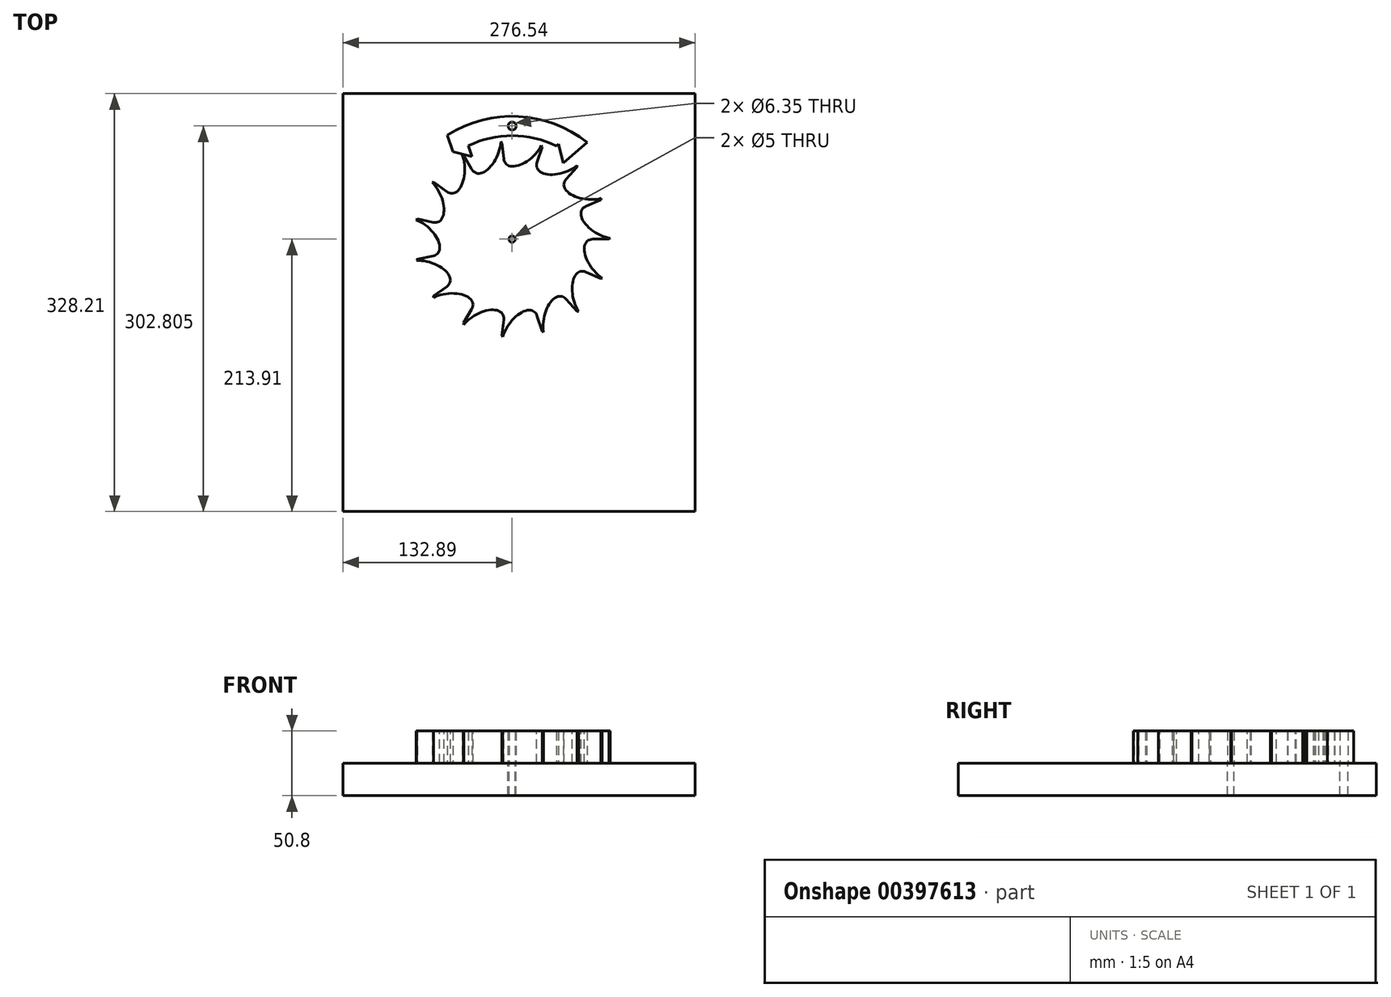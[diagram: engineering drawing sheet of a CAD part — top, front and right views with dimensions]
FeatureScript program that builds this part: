
annotation { "Feature Type Name" : "Feature", "Feature Type Description" : "" }
export const myFeature = defineFeature(function(context is Context, id is Id, definition is map)
    precondition{}
    {
        {
            var Q0;
            Q0=qCreatedBy(makeId("Top.planeOp"),FACE);
            var sketch = newSketch(context, id + "F0", { "sketchPlane" : qUnion([Q0])});
            skCircle(sketch, "E0", {"center": v(0, 0) * mm, "radius": 76.2 * mm, "construction": true});
            skCircle(sketch, "E1", {"center": v(0, 0) * mm, "radius": 95.25 * mm, "construction": true});
            skCircle(sketch, "E2", {"center": v(0, 0) * mm, "radius": 57.15 * mm, "construction": true});
            skLineSegment(sketch, "E3", {"start": v(0, 0) * mm, "end": v(-38.48, 66.66) * mm, "construction": true});
            skLineSegment(sketch, "E4", {"start": v(-104.67, 27.56) * mm, "end": v(65.84, 126) * mm, "construction": true});
            skLineSegment(sketch, "E5", {"start": v(0, 0) * mm, "end": v(-46.24, 33.6) * mm, "construction": true});
            skLineSegment(sketch, "E6", {"start": v(-96.61, 34.43) * mm, "end": v(96.61, 141.54) * mm, "construction": true});
            skPoint(sketch, "E7", {"position": v(0, 87.99) * mm});
            skPoint(sketch, "E7.positionSnap0", {"position": v(0, 87.99) * mm});
            skLineSegment(sketch, "E8", {"start": v(-38.1, 66) * mm, "end": v(-39.17, 66.28) * mm});
            skPoint(sketch, "E9", {"position": v(-51.37, 37.32) * mm});
            skPoint(sketch, "E10", {"position": v(-37.64, 60.11) * mm});
            skLineSegment(sketch, "E11.trimOffspring", {"start": v(-40.07, 69.4) * mm, "end": v(-47.63, 82.49) * mm});
            skEllipticalArc(sketch, "E12.trimOffspring", {});
            skLineSegment(sketch, "E13.trimOffspring", {"start": v(-51.37, 37.32) * mm, "end": v(-61.65, 44.79) * mm});
            skCircle(sketch, "E14", {"center": v(0, 0) * mm, "radius": 2.5 * mm});
            skLineSegment(sketch, "E15", {"start": v(0, 0) * mm, "end": v(61, 105.66) * mm, "construction": true});
            skLineSegment(sketch, "E16.1.0", {"start": v(-61.65, 44.79) * mm, "end": v(-62.74, 44.62) * mm});
            skEllipticalArc(sketch, "E16.1.1", {});
            skLineSegment(sketch, "E16.1.2", {"start": v(-62.11, 13.2) * mm, "end": v(-74.53, 15.84) * mm});
            skLineSegment(sketch, "E16.2.0", {"start": v(-74.53, 15.84) * mm, "end": v(-75.46, 15.24) * mm});
            skEllipticalArc(sketch, "E16.2.1", {});
            skLineSegment(sketch, "E16.2.2", {"start": v(-62.11, -13.2) * mm, "end": v(-74.53, -15.84) * mm});
            skEllipticalArc(sketch, "E17.3.3.0", {});
            skLineSegment(sketch, "E17.7.3.0", {"start": v(-51.37, -37.32) * mm, "end": v(-61.65, -44.79) * mm});
            skLineSegment(sketch, "E17.9.3.0", {"start": v(-74.53, -15.84) * mm, "end": v(-75.14, -16.77) * mm});
            skEllipticalArc(sketch, "E17.3.4.0", {});
            skLineSegment(sketch, "E17.7.4.0", {"start": v(-31.75, -55) * mm, "end": v(-38.1, -66) * mm});
            skLineSegment(sketch, "E17.9.4.0", {"start": v(-61.65, -44.79) * mm, "end": v(-61.82, -45.88) * mm});
            skEllipticalArc(sketch, "E17.3.5.0", {});
            skLineSegment(sketch, "E17.7.5.0", {"start": v(-6.64, -63.15) * mm, "end": v(-7.97, -75.78) * mm});
            skLineSegment(sketch, "E17.9.5.0", {"start": v(-38.1, -66) * mm, "end": v(-37.81, -67.06) * mm});
            skEllipticalArc(sketch, "E17.3.6.0", {});
            skLineSegment(sketch, "E17.7.6.0", {"start": v(19.62, -60.4) * mm, "end": v(23.55, -72.47) * mm});
            skLineSegment(sketch, "E17.9.6.0", {"start": v(-7.97, -75.78) * mm, "end": v(-7.27, -76.64) * mm});
            skEllipticalArc(sketch, "E17.3.7.0", {});
            skLineSegment(sketch, "E17.7.7.0", {"start": v(42.49, -47.19) * mm, "end": v(50.99, -56.63) * mm});
            skLineSegment(sketch, "E17.9.7.0", {"start": v(23.55, -72.47) * mm, "end": v(24.53, -72.97) * mm});
            skEllipticalArc(sketch, "E17.3.8.0", {});
            skLineSegment(sketch, "E17.7.8.0", {"start": v(58.01, -25.83) * mm, "end": v(69.61, -31) * mm});
            skLineSegment(sketch, "E17.9.8.0", {"start": v(50.99, -56.63) * mm, "end": v(52.1, -56.69) * mm});
            skEllipticalArc(sketch, "E17.3.9.0", {});
            skLineSegment(sketch, "E17.7.9.0", {"start": v(63.5, 0) * mm, "end": v(76.2, 0) * mm});
            skLineSegment(sketch, "E17.9.9.0", {"start": v(69.61, -31) * mm, "end": v(70.64, -30.6) * mm});
            skEllipticalArc(sketch, "E17.3.10.0", {});
            skLineSegment(sketch, "E17.7.10.0", {"start": v(58.01, 25.83) * mm, "end": v(69.61, 31) * mm});
            skLineSegment(sketch, "E17.9.10.0", {"start": v(76.2, 0) * mm, "end": v(76.98, 0.78) * mm});
            skEllipticalArc(sketch, "E17.3.11.0", {});
            skLineSegment(sketch, "E17.7.11.0", {"start": v(42.49, 47.19) * mm, "end": v(50.99, 56.63) * mm});
            skLineSegment(sketch, "E17.9.11.0", {"start": v(69.61, 31) * mm, "end": v(70, 32.03) * mm});
            skEllipticalArc(sketch, "E17.3.12.0", {});
            skLineSegment(sketch, "E17.7.12.0", {"start": v(19.62, 60.4) * mm, "end": v(23.55, 72.47) * mm});
            skLineSegment(sketch, "E17.9.12.0", {"start": v(50.99, 56.63) * mm, "end": v(50.93, 57.73) * mm});
            skEllipticalArc(sketch, "E17.3.13.0", {});
            skLineSegment(sketch, "E17.7.13.0", {"start": v(-6.64, 63.15) * mm, "end": v(-7.97, 75.78) * mm});
            skLineSegment(sketch, "E17.9.13.0", {"start": v(23.55, 72.47) * mm, "end": v(23.05, 73.46) * mm});
            skEllipticalArc(sketch, "E17.3.14.0", {});
            skLineSegment(sketch, "E17.7.14.0", {"start": v(-31.75, 55) * mm, "end": v(-38.1, 66) * mm});
            skLineSegment(sketch, "E17.9.14.0", {"start": v(-7.97, 75.78) * mm, "end": v(-8.82, 76.48) * mm});
            const initialGuessF0  = {"E12.trimOffspring": [-0.04789060166335672, 0.05569995491011367, 0.03374826068931686, -0.999430365208325, 0.019781070479592194, 0.010620790046448907, 5.88684132578572, 2.1170960990921337], "E16.1.1": [-0.06640545429294378, 0.03140557824359797, 0.43733552198891873, -0.8992984161037314, 0.01978107047959219, 0.010620790046448905, 5.88684132578572, 2.117096099092134], "E16.2.1": [-0.07343820060066757, 0.001680891788042732, 0.7653034984681489, -0.6436696009851731, 0.019781070479592194, 0.010620790046448907, 5.886841325785718, 2.1170960990921346], "E17.3.3.0": [-0.0677728148594282, -0.028334436128087503, 0.9609435474982175, -0.27674446430153027, 0.019781070479592194, 0.010620790046448907, 5.88684132578572, 2.117096099092134], "E17.3.4.0": [-0.05038889373229961, -0.05345048262740028, 0.9904277272677787, 0.13803230440437778, 0.019781070479592194, 0.010620790046448907, 5.88684132578572, 2.1170960990921346], "E17.3.5.0": [-0.02429227511012787, -0.06932445509804504, 0.8486579552393103, 0.5289420336946504, 0.019781070479592194, 0.010620790046448907, 5.88684132578572, 2.117096099092134], "E17.3.6.0": [0.006004698566976163, -0.07321159948933473, 0.5601475129344807, 0.8283928800715973, 0.019781070479592194, 0.010620790046448907, 5.886841325785721, 2.1170960990921337], "E17.3.7.0": [0.03526340531087609, -0.06443979322241714, 0.17478247686287926, 0.9846070717711087, 0.019781070479592194, 0.010620790046448907, 5.88684132578572, 2.117096099092134], "E17.3.8.0": [0.058424748918545454, -0.04452576129020056, -0.24080403730726763, 0.9705737558869599, 0.019781070479592194, 0.010620790046448907, 5.88684132578572, 2.117096099092134], "E17.3.9.0": [0.07148392266601725, -0.016912820727065802, -0.6147533457909872, 0.7887194202241931, 0.019781070479592194, 0.010620790046448907, 5.88684132578572, 2.1170960990921346], "E17.3.10.0": [0.07218287677348459, 0.013624500187931342, -0.8824062159286269, 0.47048833151367486, 0.019781070479592194, 0.010620790046448907, 5.88684132578572, 2.1170960990921337], "E17.3.11.0": [0.06040075572596765, 0.041806021245736694, -0.9974830349233995, 0.07090553603213468, 0.019781070479592194, 0.010620790046448907, 5.88684132578572, 2.117096099092134], "E17.3.12.0": [0.0381747952897915, 0.06275890143437435, -0.9400859753310279, -0.34093747078593484, 0.019781070479592194, 0.010620790046448907, 5.88684132578572, 2.1170960990921337], "E17.3.13.0": [0.0093480659408827, 0.07286019741828806, -0.7201395101909495, -0.6938292915854298, 0.019781070479592194, 0.010620790046448907, 5.88684132578572, 2.117096099092134], "E17.3.14.0": [-0.021095028933717657, 0.07036330335446608, -0.37567438147679133, -0.9267517246285708, 0.019781070479592194, 0.010620790046448907, 5.886841325785721, 2.1170960990921337]};
            skSetInitialGuess(sketch, initialGuessF0);
            skSolve(sketch);
        }
        {
            var Q0;
            Q0=qSketchRegion(id+"F0",true);
            extrude(context, id + "F1", {"entities" : qUnion([Q0]), "depth" : 25.4 * mm});
        }
        {
            var Q0;
            Q0=qCreatedBy(makeId("Top.planeOp"),FACE);
            var sketch = newSketch(context, id + "F2", { "sketchPlane" : qUnion([Q0])});
            skLineSegment(sketch, "E18", {"start": v(-41.75, 72.3) * mm, "end": v(0, 0) * mm, "construction": true});
            skLineSegment(sketch, "E19", {"start": v(0, 0) * mm, "end": v(41.8, 72.41) * mm, "construction": true});
            skCircle(sketch, "E20", {"center": v(0, 0) * mm, "radius": 76.99 * mm, "construction": true});
            skLineSegment(sketch, "E21", {"start": v(-38.5, 66.67) * mm, "end": v(0, 88.9) * mm, "construction": true});
            skLineSegment(sketch, "E22", {"start": v(0, 88.9) * mm, "end": v(38.5, 66.67) * mm, "construction": true});
            skLineSegment(sketch, "E23", {"start": v(0, 0) * mm, "end": v(-44.19, 90.6) * mm, "construction": true});
            skLineSegment(sketch, "E24", {"start": v(0, 0) * mm, "end": v(-56.37, 83.56) * mm, "construction": true});
            skLineSegment(sketch, "E25", {"start": v(0, 88.9) * mm, "end": v(-127.8, 129.79) * mm, "construction": true});
            skLineSegment(sketch, "E26", {"start": v(0, 88.9) * mm, "end": v(-28.48, -42.22) * mm, "construction": true});
            skLineSegment(sketch, "E27", {"start": v(0, 88.9) * mm, "end": v(130.35, 25.32) * mm, "construction": true});
            skLineSegment(sketch, "E28", {"start": v(0, 88.9) * mm, "end": v(120.23, 7.8) * mm, "construction": true});
            skLineSegment(sketch, "E29", {"start": v(0, 0) * mm, "end": v(48.31, 99.05) * mm, "construction": true});
            skLineSegment(sketch, "E30", {"start": v(0, 0) * mm, "end": v(61.63, 91.36) * mm, "construction": true});
            skLineSegment(sketch, "E31", {"start": v(-46.4, 68.8) * mm, "end": v(-31.62, 64.83) * mm});
            skPoint(sketch, "E32", {"position": v(-38.5, 66.67) * mm});
            skLineSegment(sketch, "E33", {"start": v(-46.4, 68.8) * mm, "end": v(-50.8, 81.6) * mm});
            skLineSegment(sketch, "E34", {"start": v(-31.62, 64.83) * mm, "end": v(-34.54, 73.3) * mm});
            skLineSegment(sketch, "E35", {"start": v(36.37, 74.58) * mm, "end": v(40.33, 59.8) * mm});
            skPoint(sketch, "E36", {"position": v(38.5, 66.67) * mm});
            skLineSegment(sketch, "E37", {"start": v(40.33, 59.8) * mm, "end": v(58.8, 75.85) * mm});
            skLineSegment(sketch, "E38", {"start": v(36.37, 74.58) * mm, "end": v(34.77, 73.18) * mm});
            skArc(sketch, "E39", {"start": v(58.8, 75.85) * mm, "mid": v(4.92, 96.39) * mm, "end": v(-50.8, 81.6) * mm});
            skArc(sketch, "E40.trimOffspring", {"start": v(34.77, 73.18) * mm, "mid": v(0.13, 81.28) * mm, "end": v(-34.54, 73.3) * mm});
            skCircle(sketch, "E41", {"center": v(0, 88.9) * mm, "radius": 3.18 * mm});
            skLineSegment(sketch, "E42.0", {"start": v(-7.97, 75.78) * mm, "end": v(-8.82, 76.48) * mm});
            skSolve(sketch);
        }
        {
            var Q0;
            Q0=makeQuery(id+"F2.imprint","IMPRINT",FACE,{"disambiguationData":[TD([[makeQuery(id+"F2.imprint","IMPRINT",EDGE,{"derivedFrom":sQuery(id+"F2.wireOp",EDGE,"E31")}),1.0]])]});
            extrude(context, id + "F3", {"entities" : qUnion([Q0]), "depth" : 25.4 * mm});
        }
        {
            var Q0;
            Q0=qCreatedBy(makeId("Top.planeOp"),FACE);
            var sketch = newSketch(context, id + "F4", { "sketchPlane" : qUnion([Q0])});
            skLineSegment(sketch, "E43.bottom", {"start": v(-132.9, 114.3) * mm, "end": v(143.65, 114.3) * mm});
            skLineSegment(sketch, "E43.top", {"start": v(-132.9, -213.91) * mm, "end": v(143.65, -213.91) * mm});
            skLineSegment(sketch, "E43.left", {"start": v(-132.9, 114.3) * mm, "end": v(-132.9, -213.91) * mm});
            skLineSegment(sketch, "E43.right", {"start": v(143.65, 114.3) * mm, "end": v(143.65, -213.91) * mm});
            skCircle(sketch, "E44.0", {"center": v(0, 88.9) * mm, "radius": 3.18 * mm});
            skCircle(sketch, "E45.0", {"center": v(0, 0) * mm, "radius": 2.5 * mm});
            skSolve(sketch);
        }
        {
            var Q0;
            Q0=makeQuery(id+"F4.imprint","IMPRINT",FACE,{"disambiguationData":[TD([[makeQuery(id+"F4.imprint","IMPRINT",EDGE,{"derivedFrom":sQuery(id+"F4.wireOp",EDGE,"E43.bottom")}),-1.0]])]});
            extrude(context, id + "F5", {"entities" : qUnion([Q0]), "oppositeDirection" : true, "depth" : 25.4 * mm});
        }
    });
